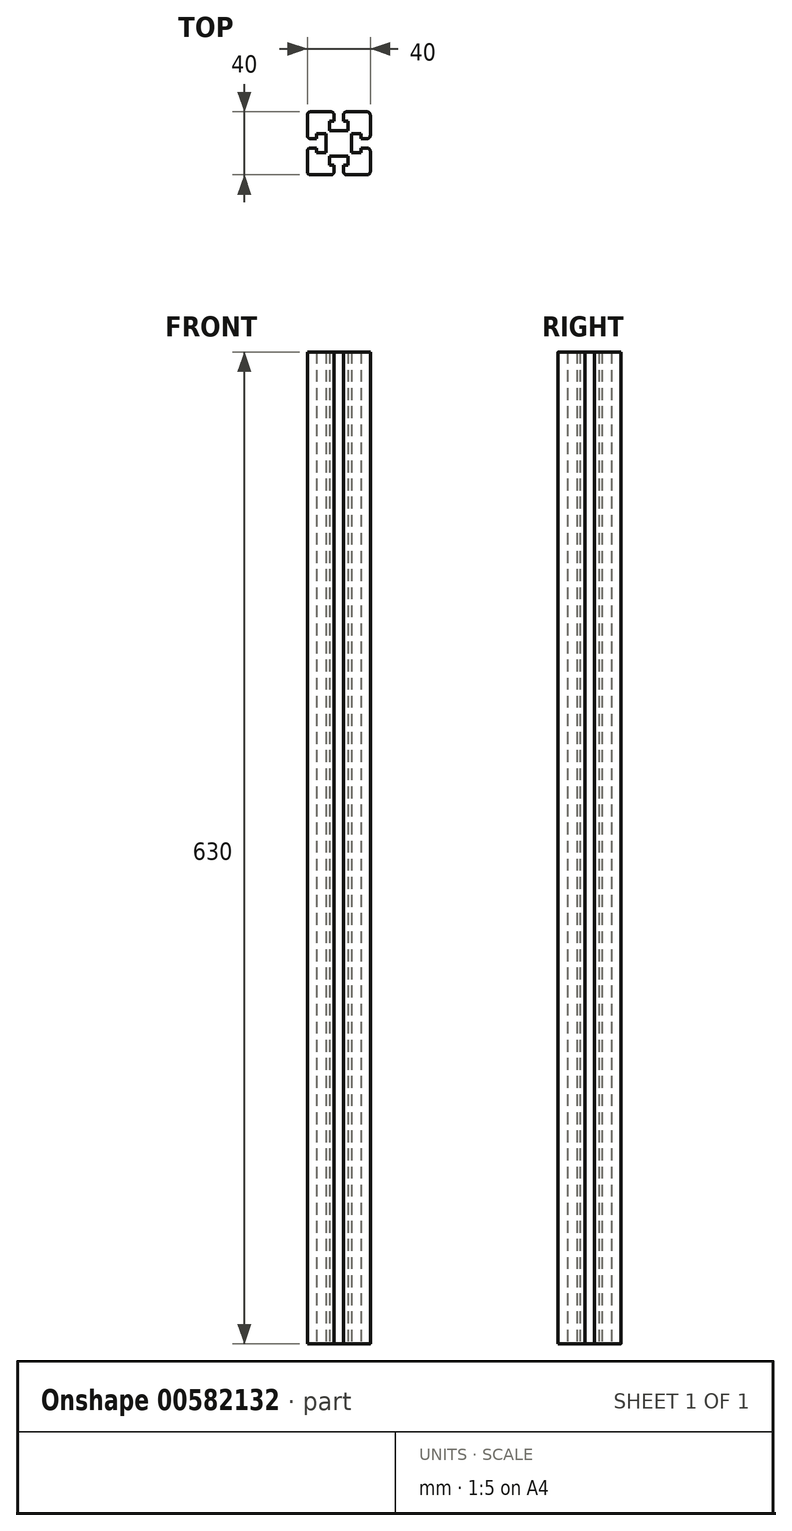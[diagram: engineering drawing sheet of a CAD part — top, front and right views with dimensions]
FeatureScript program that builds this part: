
annotation { "Feature Type Name" : "Feature", "Feature Type Description" : "" }
export const myFeature = defineFeature(function(context is Context, id is Id, definition is map)
    precondition{}
    {
        {
            var Q0;
            Q0=qCreatedBy(makeId("Top.planeOp"),FACE);
            var sketch = newSketch(context, id + "F0", { "sketchPlane" : qUnion([Q0])});
            skLineSegment(sketch, "E0.bottom", {"start": v(20, 20) * mm, "end": v(3, 20) * mm});
            skLineSegment(sketch, "E0.top", {"start": v(20, -20) * mm, "end": v(3, -20) * mm});
            skLineSegment(sketch, "E0.left", {"start": v(20, 20) * mm, "end": v(20, 3) * mm});
            skLineSegment(sketch, "E0.right", {"start": v(-20, 20) * mm, "end": v(-20, 3) * mm});
            skPoint(sketch, "E0.middle", {"position": v(0, 0) * mm});
            skLineSegment(sketch, "E1.left", {"start": v(3, 14) * mm, "end": v(3, 20) * mm});
            skLineSegment(sketch, "E1.right", {"start": v(-3, 14) * mm, "end": v(-3, 20) * mm});
            skPoint(sketch, "E1.middle", {"position": v(0, 20) * mm});
            skLineSegment(sketch, "E2.bottom", {"start": v(-6, 14) * mm, "end": v(-3, 14) * mm});
            skLineSegment(sketch, "E2.top", {"start": v(-6, 8) * mm, "end": v(6, 8) * mm});
            skLineSegment(sketch, "E2.left", {"start": v(-6, 14) * mm, "end": v(-6, 8) * mm});
            skLineSegment(sketch, "E2.right", {"start": v(6, 14) * mm, "end": v(6, 8) * mm});
            skPoint(sketch, "E2.middle", {"position": v(0, 11) * mm});
            skLineSegment(sketch, "E3.bottom", {"start": v(14, 3) * mm, "end": v(20, 3) * mm});
            skLineSegment(sketch, "E3.top", {"start": v(14, -3) * mm, "end": v(20, -3) * mm});
            skPoint(sketch, "E3.middle", {"position": v(20, 0) * mm});
            skLineSegment(sketch, "E4.bottom", {"start": v(14, 6) * mm, "end": v(8, 6) * mm});
            skLineSegment(sketch, "E4.top", {"start": v(14, -6) * mm, "end": v(8, -6) * mm});
            skLineSegment(sketch, "E4.left", {"start": v(14, 6) * mm, "end": v(14, 3) * mm});
            skLineSegment(sketch, "E4.right", {"start": v(8, 6) * mm, "end": v(8, -6) * mm});
            skPoint(sketch, "E4.middle", {"position": v(11, 0) * mm});
            skPoint(sketch, "E4.middle.positionSnap0", {"position": v(14, 0) * mm});
            skPoint(sketch, "E4.centerSnap0", {"position": v(14, 0) * mm});
            skLineSegment(sketch, "E5.left", {"start": v(3.1, -14) * mm, "end": v(3, -20) * mm});
            skLineSegment(sketch, "E5.right", {"start": v(-2.9, -14) * mm, "end": v(-3, -20) * mm});
            skPoint(sketch, "E5.middle", {"position": v(0, -20) * mm});
            skLineSegment(sketch, "E6.bottom", {"start": v(6, -14) * mm, "end": v(3.1, -14) * mm});
            skLineSegment(sketch, "E6.top", {"start": v(6, -8) * mm, "end": v(-6, -8) * mm});
            skLineSegment(sketch, "E6.left", {"start": v(6, -14) * mm, "end": v(6, -8) * mm});
            skLineSegment(sketch, "E6.right", {"start": v(-6, -14) * mm, "end": v(-6, -8) * mm});
            skPoint(sketch, "E6.middle", {"position": v(0, -11) * mm});
            skLineSegment(sketch, "E7.bottom", {"start": v(-14, -3) * mm, "end": v(-20, -3) * mm});
            skLineSegment(sketch, "E7.top", {"start": v(-14, 3) * mm, "end": v(-20, 3) * mm});
            skPoint(sketch, "E7.middle", {"position": v(-20, 0) * mm});
            skLineSegment(sketch, "E8.bottom", {"start": v(-14, 6) * mm, "end": v(-8, 6) * mm});
            skLineSegment(sketch, "E8.top", {"start": v(-14, -6) * mm, "end": v(-8, -6) * mm});
            skLineSegment(sketch, "E8.left", {"start": v(-14, 6) * mm, "end": v(-14, 3) * mm});
            skLineSegment(sketch, "E8.right", {"start": v(-8, 6) * mm, "end": v(-8, -6) * mm});
            skPoint(sketch, "E8.middle", {"position": v(-11, 0) * mm});
            skPoint(sketch, "E8.cornerSnap0", {"position": v(-14, 0) * mm});
            skPoint(sketch, "E9.orphan", {"position": v(-3, 26) * mm});
            skPoint(sketch, "E10.orphan", {"position": v(3, 26) * mm});
            skLineSegment(sketch, "E11.trimOffspring", {"start": v(-3, 20) * mm, "end": v(-20, 20) * mm});
            skLineSegment(sketch, "E12.trimOffspring", {"start": v(3, 14) * mm, "end": v(6, 14) * mm});
            skLineSegment(sketch, "E13.trimOffspring", {"start": v(14, -3) * mm, "end": v(14, -6) * mm});
            skLineSegment(sketch, "E14.trimOffspring", {"start": v(20, -3) * mm, "end": v(20, -20) * mm});
            skPoint(sketch, "E3.right.start.orphan", {"position": v(26, 3) * mm});
            skPoint(sketch, "E15.orphan", {"position": v(26, -3) * mm});
            skLineSegment(sketch, "E16.trimOffspring", {"start": v(-14, -3) * mm, "end": v(-14, -6) * mm});
            skPoint(sketch, "E7.right.end.orphan", {"position": v(-26, 3) * mm});
            skPoint(sketch, "E17.orphan", {"position": v(-26, -3) * mm});
            skLineSegment(sketch, "E18.trimOffspring", {"start": v(-20, -3) * mm, "end": v(-20, -20) * mm});
            skLineSegment(sketch, "E19.trimOffspring", {"start": v(-2.9, -14) * mm, "end": v(-6, -14) * mm});
            skLineSegment(sketch, "E20.trimOffspring", {"start": v(-3, -20) * mm, "end": v(-20, -20) * mm});
            skPoint(sketch, "E21.orphan", {"position": v(-3.1, -26) * mm});
            skPoint(sketch, "E22.orphan", {"position": v(2.9, -26) * mm});
            skSolve(sketch);
        }
        {
            var Q0;
            Q0=qSketchRegion(id+"F0",true);
            extrude(context, id + "F1", {"entities" : qUnion([Q0]), "depth" : 630 * mm, "offsetDistance" : 25 * mm});
        }
        {
            var Q0;
            Q0=makeQuery(id+"F1.opExtrude","SWEPT_EDGE",EDGE,{"disambiguationData":[OSD([sQuery(id+"F0.wireOp",EDGE,"E0.left"),sQuery(id+"F0.wireOp",EDGE,"E3.bottom")])]});
            var Q1;
            Q1=makeQuery(id+"F1.opExtrude","SWEPT_EDGE",EDGE,{"disambiguationData":[OSD([sQuery(id+"F0.wireOp",EDGE,"E0.bottom"),sQuery(id+"F0.wireOp",EDGE,"E0.left")])]});
            var Q2;
            Q2=makeQuery(id+"F1.opExtrude","SWEPT_EDGE",EDGE,{"disambiguationData":[OSD([sQuery(id+"F0.wireOp",EDGE,"E0.top"),sQuery(id+"F0.wireOp",EDGE,"E14.trimOffspring")])]});
            var Q3;
            Q3=makeQuery(id+"F1.opExtrude","SWEPT_EDGE",EDGE,{"disambiguationData":[OSD([sQuery(id+"F0.wireOp",EDGE,"E3.top"),sQuery(id+"F0.wireOp",EDGE,"E14.trimOffspring")])]});
            var Q4;
            Q4=makeQuery(id+"F1.opExtrude","SWEPT_EDGE",EDGE,{"disambiguationData":[OSD([sQuery(id+"F0.wireOp",EDGE,"E5.right"),sQuery(id+"F0.wireOp",EDGE,"E20.trimOffspring")])]});
            var Q5;
            Q5=makeQuery(id+"F1.opExtrude","SWEPT_EDGE",EDGE,{"disambiguationData":[OSD([sQuery(id+"F0.wireOp",EDGE,"E1.right"),sQuery(id+"F0.wireOp",EDGE,"E11.trimOffspring")])]});
            var Q6;
            Q6=makeQuery(id+"F1.opExtrude","SWEPT_EDGE",EDGE,{"disambiguationData":[OSD([sQuery(id+"F0.wireOp",EDGE,"E0.bottom"),sQuery(id+"F0.wireOp",EDGE,"E1.left")])]});
            var Q7;
            Q7=makeQuery(id+"F1.opExtrude","SWEPT_EDGE",EDGE,{"disambiguationData":[OSD([sQuery(id+"F0.wireOp",EDGE,"E0.right"),sQuery(id+"F0.wireOp",EDGE,"E11.trimOffspring")])]});
            var Q8;
            Q8=makeQuery(id+"F1.opExtrude","SWEPT_EDGE",EDGE,{"disambiguationData":[OSD([sQuery(id+"F0.wireOp",EDGE,"E7.bottom"),sQuery(id+"F0.wireOp",EDGE,"E18.trimOffspring")])]});
            var Q9;
            Q9=makeQuery(id+"F1.opExtrude","SWEPT_EDGE",EDGE,{"disambiguationData":[OSD([sQuery(id+"F0.wireOp",EDGE,"E0.right"),sQuery(id+"F0.wireOp",EDGE,"E7.top")])]});
            var Q10;
            Q10=makeQuery(id+"F1.opExtrude","SWEPT_EDGE",EDGE,{"disambiguationData":[OSD([sQuery(id+"F0.wireOp",EDGE,"E18.trimOffspring"),sQuery(id+"F0.wireOp",EDGE,"E20.trimOffspring")])]});
            var Q11;
            Q11=makeQuery(id+"F1.opExtrude","SWEPT_EDGE",EDGE,{"disambiguationData":[OSD([sQuery(id+"F0.wireOp",EDGE,"E0.top"),sQuery(id+"F0.wireOp",EDGE,"E5.left")])]});
            fillet(context, id + "F2", {"entities" : qUnion([Q0, Q1, Q2, Q3, Q4, Q5, Q6, Q7, Q8, Q9, Q10, Q11]), "radius" : 2 * mm, "tangentPropagation" : true, "allowEdgeOverflow" : false});
        }
    });
